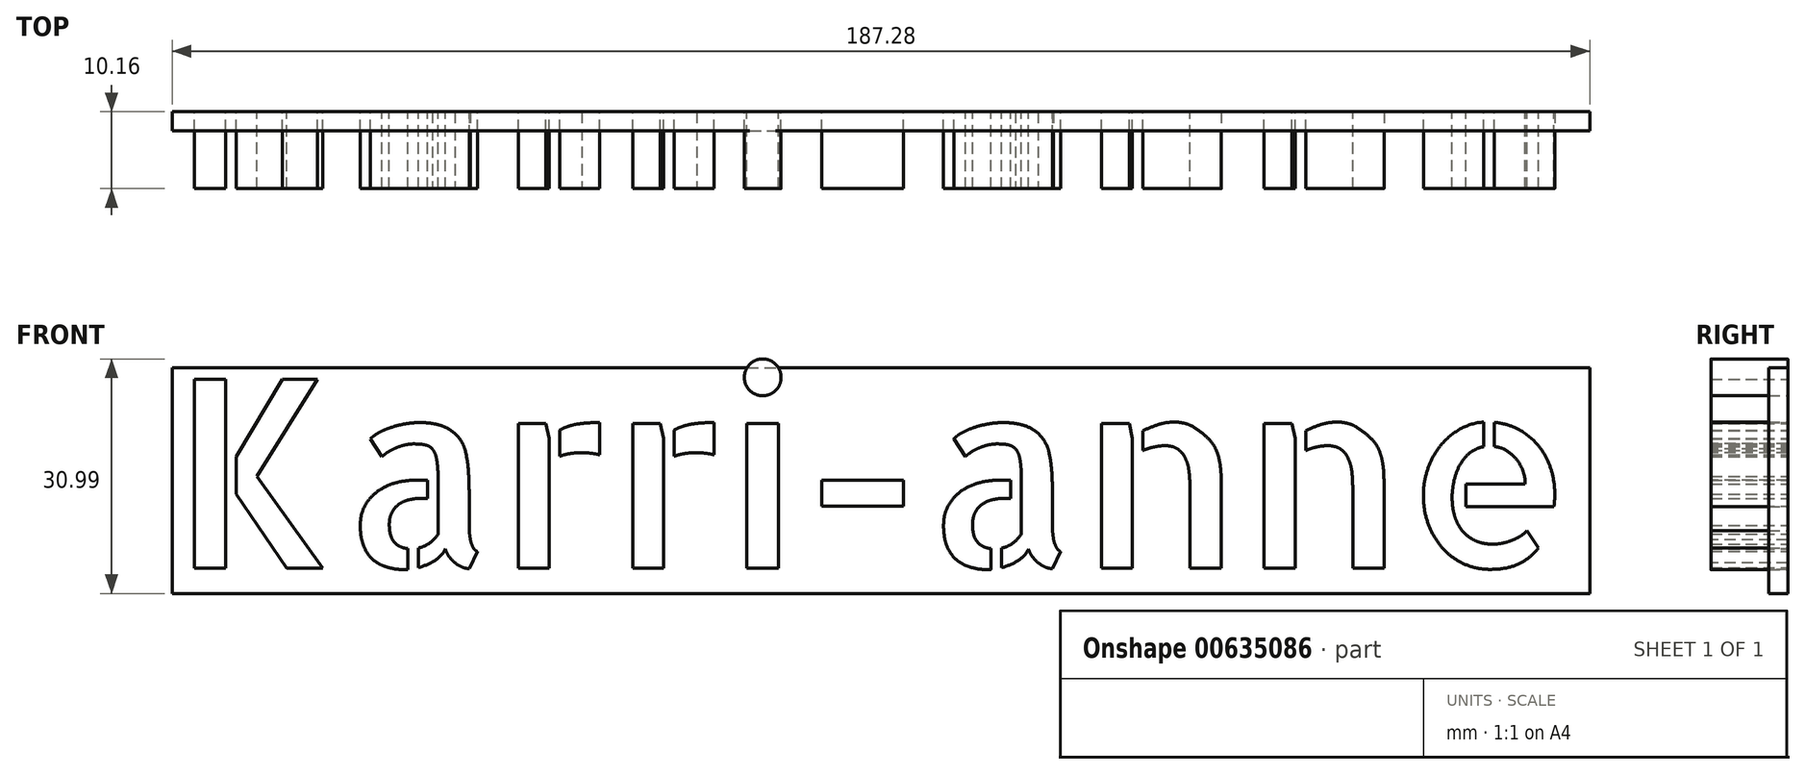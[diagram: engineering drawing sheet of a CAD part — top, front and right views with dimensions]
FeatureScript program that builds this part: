
annotation { "Feature Type Name" : "Feature", "Feature Type Description" : "" }
export const myFeature = defineFeature(function(context is Context, id is Id, definition is map)
    precondition{}
    {
        {
            var Q0;
            Q0=qCreatedBy(makeId("Front.planeOp"),FACE);
            var sketch = newSketch(context, id + "F0", { "sketchPlane" : qUnion([Q0])});
            skText(sketch, "E0", { "text": "Karri-anne", "fontName": "AllertaStencil-Regular.ttf"});
            const initialGuessF0  = {"E0": [-0.04691, 0, 1, 0, 0.025]};
            skSetInitialGuess(sketch, initialGuessF0);
            skSolve(sketch);
        }
        {
            var Q0;
            Q0 = qSketchRegion(id + "F0", true);
            extrude(context, id + "F1", {"entities" : qUnion([Q0]), "depth" : 10.16 * mm, "offsetDistance" : 25.4 * mm});
        }
        {
            var Q0;
            Q0=qCreatedBy(makeId("Front.planeOp"),FACE);
            var sketch = newSketch(context, id + "F2", { "sketchPlane" : qUnion([Q0])});
            skLineSegment(sketch, "E1.bottom", {"start": v(-46.71, 26.52) * mm, "end": v(140.57, 26.52) * mm});
            skLineSegment(sketch, "E1.top", {"start": v(-46.71, -3.32) * mm, "end": v(140.57, -3.32) * mm});
            skLineSegment(sketch, "E1.left", {"start": v(-46.71, 26.52) * mm, "end": v(-46.71, -3.32) * mm});
            skLineSegment(sketch, "E1.right", {"start": v(140.57, 26.52) * mm, "end": v(140.57, -3.32) * mm});
            skSolve(sketch);
        }
        {
            var Q0;
            Q0=makeQuery(id+"F2.imprint","IMPRINT",FACE,{"disambiguationData":[TD([[makeQuery(id+"F2.imprint","IMPRINT",EDGE,{"derivedFrom":sQuery(id+"F2.wireOp",EDGE,"E1.bottom")}),-1.0]])]});
            extrude(context, id + "F3", {"entities" : qUnion([Q0]), "depth" : 2.54 * mm, "offsetDistance" : 25.4 * mm});
        }
    });
